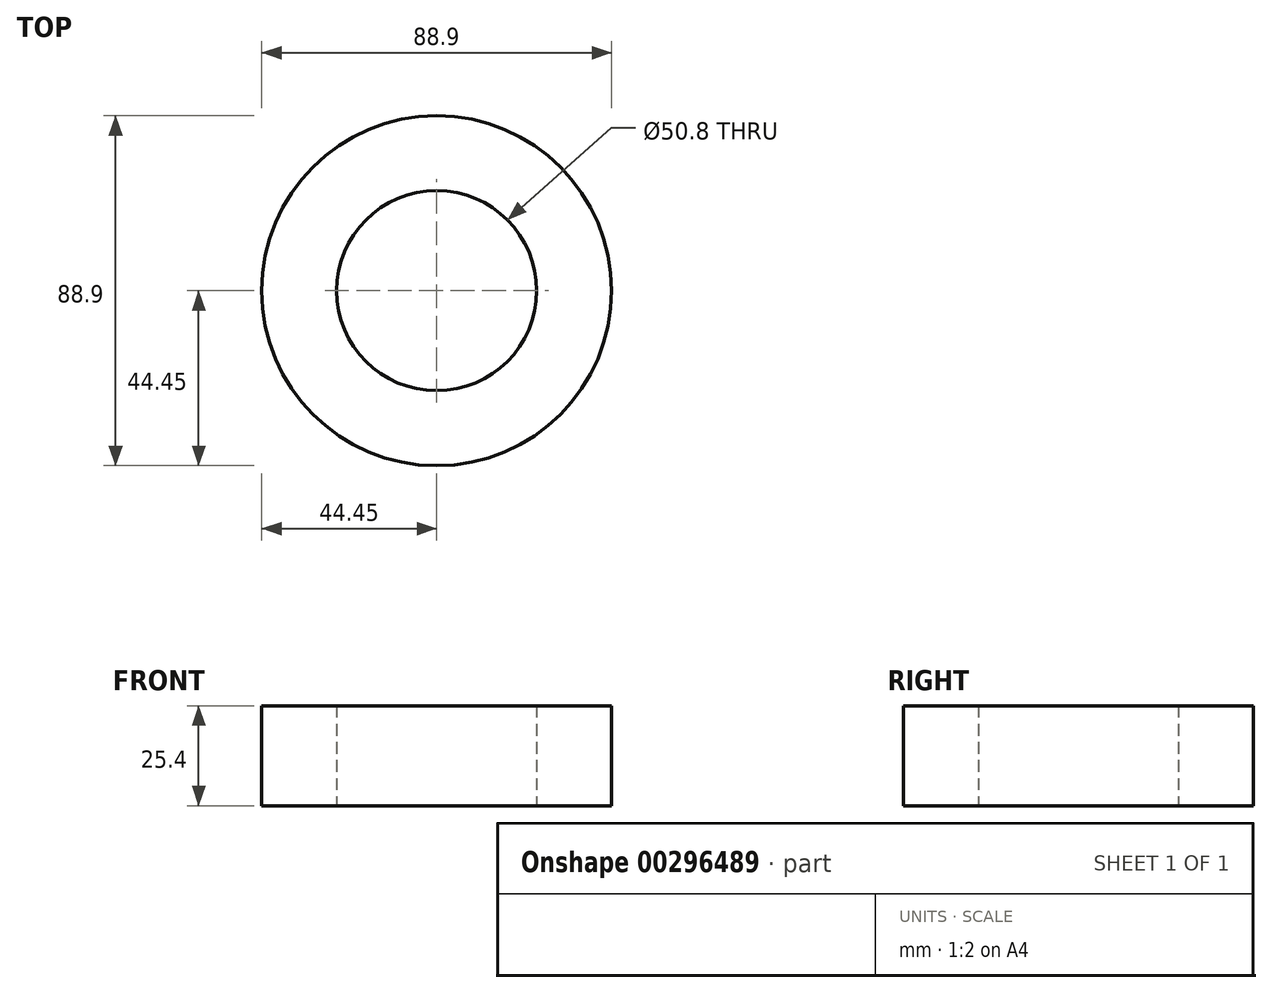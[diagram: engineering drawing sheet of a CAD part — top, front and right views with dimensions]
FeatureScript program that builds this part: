
annotation { "Feature Type Name" : "Feature", "Feature Type Description" : "" }
export const myFeature = defineFeature(function(context is Context, id is Id, definition is map)
    precondition{}
    {
        {
            var Q0;
            Q0=qCreatedBy(makeId("Top.planeOp"),FACE);
            var sketch = newSketch(context, id + "F0", { "sketchPlane" : qUnion([Q0])});
            skCircle(sketch, "E0", {"center": v(0, 0) * mm, "radius": 44.45 * mm});
            skCircle(sketch, "E1", {"center": v(0, 0) * mm, "radius": 25.4 * mm});
            skSolve(sketch);
        }
        {
            var Q0;
            Q0=makeQuery(id+"F0.imprint","IMPRINT",FACE,{"disambiguationData":[TD([[makeQuery(id+"F0.imprint","IMPRINT",EDGE,{"derivedFrom":sQuery(id+"F0.wireOp",EDGE,"E0")}),1.0]])]});
            extrude(context, id + "F1", {"entities" : qUnion([Q0]), "depth" : 25.4 * mm});
        }
    });
